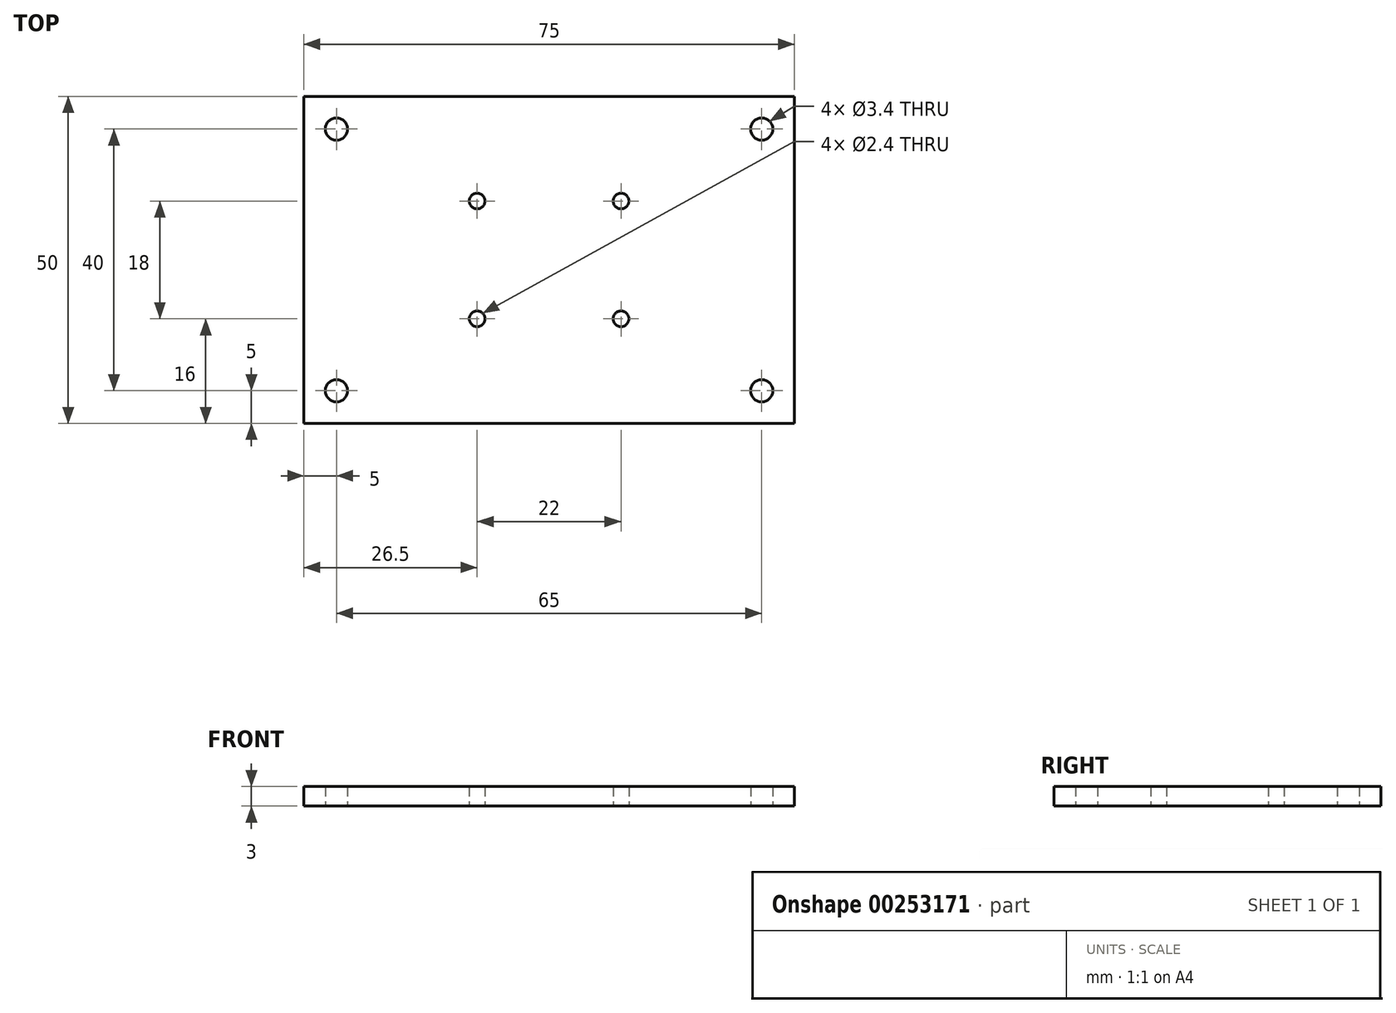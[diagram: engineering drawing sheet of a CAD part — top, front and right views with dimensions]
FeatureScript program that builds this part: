
annotation { "Feature Type Name" : "Feature", "Feature Type Description" : "" }
export const myFeature = defineFeature(function(context is Context, id is Id, definition is map)
    precondition{}
    {
        {
            var Q0;
            Q0=qCreatedBy(makeId("Top.planeOp"),FACE);
            var sketch = newSketch(context, id + "F0", { "sketchPlane" : qUnion([Q0])});
            skLineSegment(sketch, "E0.bottom", {"start": v(-37.5, 25) * mm, "end": v(37.5, 25) * mm});
            skLineSegment(sketch, "E0.top", {"start": v(-37.5, -25) * mm, "end": v(37.5, -25) * mm});
            skLineSegment(sketch, "E0.left", {"start": v(-37.5, 25) * mm, "end": v(-37.5, -25) * mm});
            skLineSegment(sketch, "E0.right", {"start": v(37.5, 25) * mm, "end": v(37.5, -25) * mm});
            skLineSegment(sketch, "E1", {"start": v(-32.5, 33.37) * mm, "end": v(-32.5, -53.54) * mm, "construction": true});
            skLineSegment(sketch, "E2", {"start": v(32.5, 42.22) * mm, "end": v(32.5, -44.7) * mm, "construction": true});
            skLineSegment(sketch, "E3", {"start": v(-53.48, 20) * mm, "end": v(58.34, 20) * mm, "construction": true});
            skLineSegment(sketch, "E4", {"start": v(-55.37, -20) * mm, "end": v(63.45, -20) * mm, "construction": true});
            skCircle(sketch, "E5", {"center": v(-32.5, 20) * mm, "radius": 1.7 * mm});
            skCircle(sketch, "E6", {"center": v(32.5, 20) * mm, "radius": 1.7 * mm});
            skCircle(sketch, "E7", {"center": v(-32.5, -20) * mm, "radius": 1.7 * mm});
            skCircle(sketch, "E8", {"center": v(32.5, -20) * mm, "radius": 1.7 * mm});
            skLineSegment(sketch, "E9", {"start": v(-11, -9) * mm, "end": v(11, -9) * mm, "construction": true});
            skLineSegment(sketch, "E10", {"start": v(11, -9) * mm, "end": v(11, 9) * mm, "construction": true});
            skLineSegment(sketch, "E11", {"start": v(11, 9) * mm, "end": v(-11, 9) * mm, "construction": true});
            skCircle(sketch, "E12", {"center": v(-11, 9) * mm, "radius": 1.2 * mm});
            skCircle(sketch, "E13", {"center": v(11, 9) * mm, "radius": 1.2 * mm});
            skCircle(sketch, "E14", {"center": v(11, -9) * mm, "radius": 1.2 * mm});
            skCircle(sketch, "E15", {"center": v(-11, -9) * mm, "radius": 1.2 * mm});
            skSolve(sketch);
        }
        {
            var Q0;
            Q0=makeQuery(id+"F0.imprint","IMPRINT",FACE,{"disambiguationData":[TD([[makeQuery(id+"F0.imprint","IMPRINT",EDGE,{"derivedFrom":sQuery(id+"F0.wireOp",EDGE,"E0.bottom")}),-1.0]])]});
            extrude(context, id + "F1", {"entities" : qUnion([Q0]), "depth" : 3 * mm});
        }
    });
